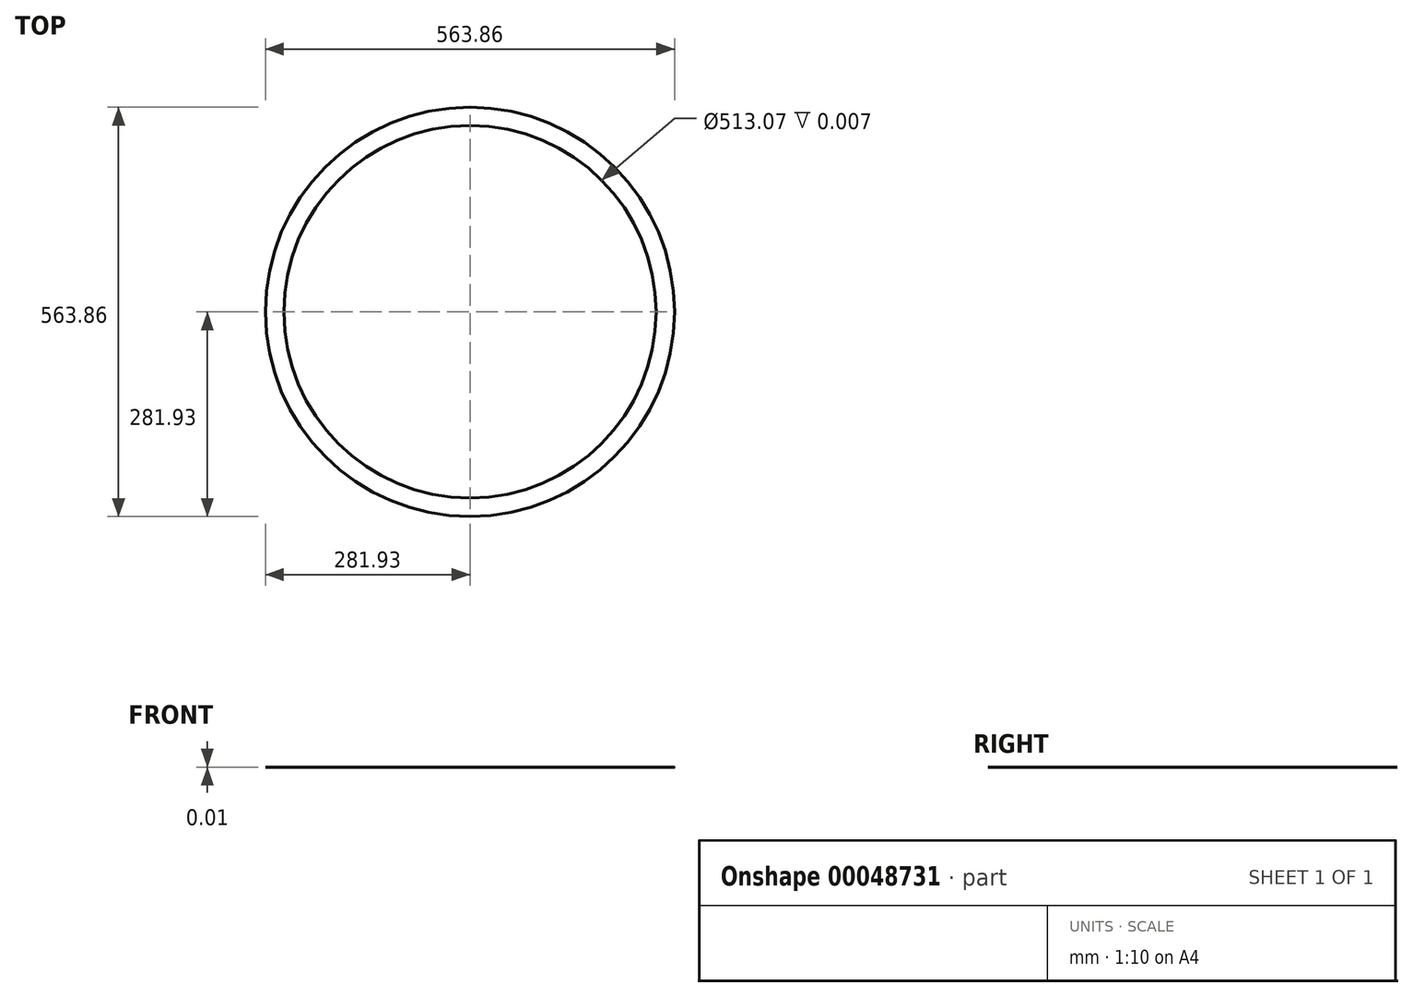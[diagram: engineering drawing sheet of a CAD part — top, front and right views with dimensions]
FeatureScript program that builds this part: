
annotation { "Feature Type Name" : "Feature", "Feature Type Description" : "" }
export const myFeature = defineFeature(function(context is Context, id is Id, definition is map)
    precondition{}
    {
        {
            var Q0;
            Q0=qCreatedBy(makeId("Top.planeOp"),FACE);
            var sketch = newSketch(context, id + "F0", { "sketchPlane" : qUnion([Q0])});
            skCircle(sketch, "E0", {"center": v(0, 0) * mm, "radius": 281.93 * mm});
            skCircle(sketch, "E1", {"center": v(0, 0) * mm, "radius": 256.53 * mm});
            skSolve(sketch);
        }
        {
            var Q0;
            Q0=makeQuery(id+"F0.imprint","IMPRINT",FACE,{"disambiguationData":[TD([[makeQuery(id+"F0.imprint","IMPRINT",EDGE,{"derivedFrom":sQuery(id+"F0.wireOp",EDGE,"E0")}),1.0]])]});
            extrude(context, id + "F1", {"entities" : qUnion([Q0]), "depth" : 3 / 406.4 * mm});
        }
    });
